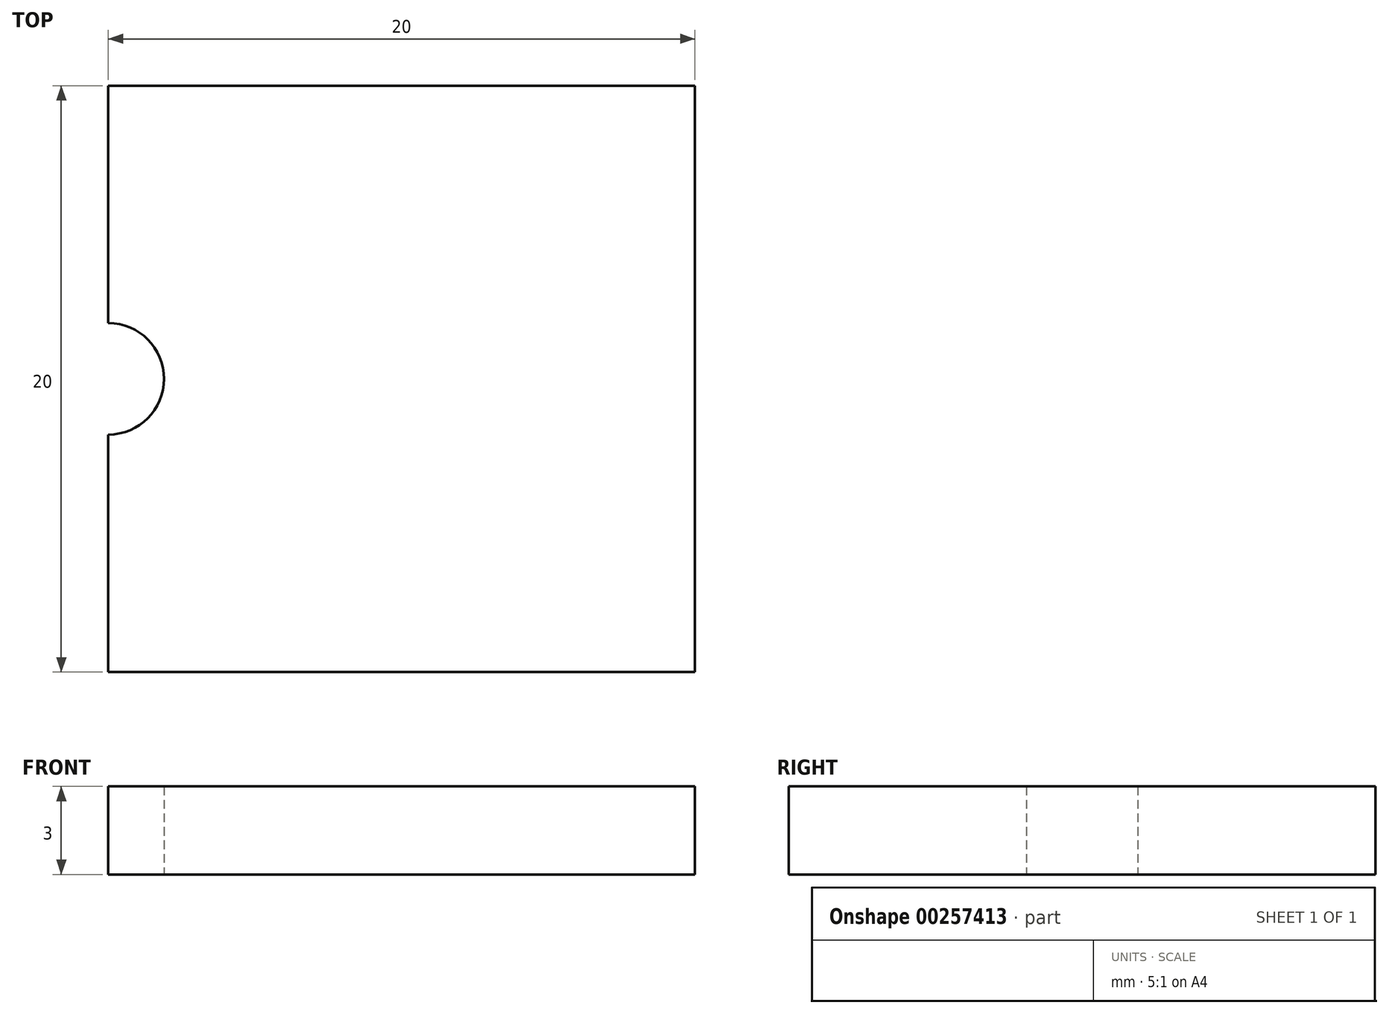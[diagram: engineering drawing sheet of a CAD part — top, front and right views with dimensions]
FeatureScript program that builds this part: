
annotation { "Feature Type Name" : "Feature", "Feature Type Description" : "" }
export const myFeature = defineFeature(function(context is Context, id is Id, definition is map)
    precondition{}
    {
        {
            var Q0;
            Q0=qCreatedBy(makeId("Top.planeOp"),FACE);
            var sketch = newSketch(context, id + "F0", { "sketchPlane" : qUnion([Q0])});
            skArc(sketch, "E0", {"start": v(0, -1.9) * mm, "mid": v(1.9, 0) * mm, "end": v(0, 1.9) * mm});
            skLineSegment(sketch, "E1.bottom", {"start": v(0, 10) * mm, "end": v(20, 10) * mm});
            skLineSegment(sketch, "E1.top", {"start": v(0, -10) * mm, "end": v(20, -10) * mm});
            skLineSegment(sketch, "E1.right", {"start": v(20, 10) * mm, "end": v(20, -10) * mm});
            skLineSegment(sketch, "E2", {"start": v(0, 10) * mm, "end": v(0, 1.9) * mm});
            skLineSegment(sketch, "E3", {"start": v(0, -1.9) * mm, "end": v(0, -10) * mm});
            skPoint(sketch, "E1.left.start.orphan", {"position": v(-20, 10) * mm});
            skPoint(sketch, "E4.orphan", {"position": v(-20, -10) * mm});
            skSolve(sketch);
        }
        {
            var Q0;
            Q0 = qSketchRegion(id + "F0", true);
            extrude(context, id + "F1", {"entities" : qUnion([Q0]), "depth" : 3 * mm});
        }
    });
